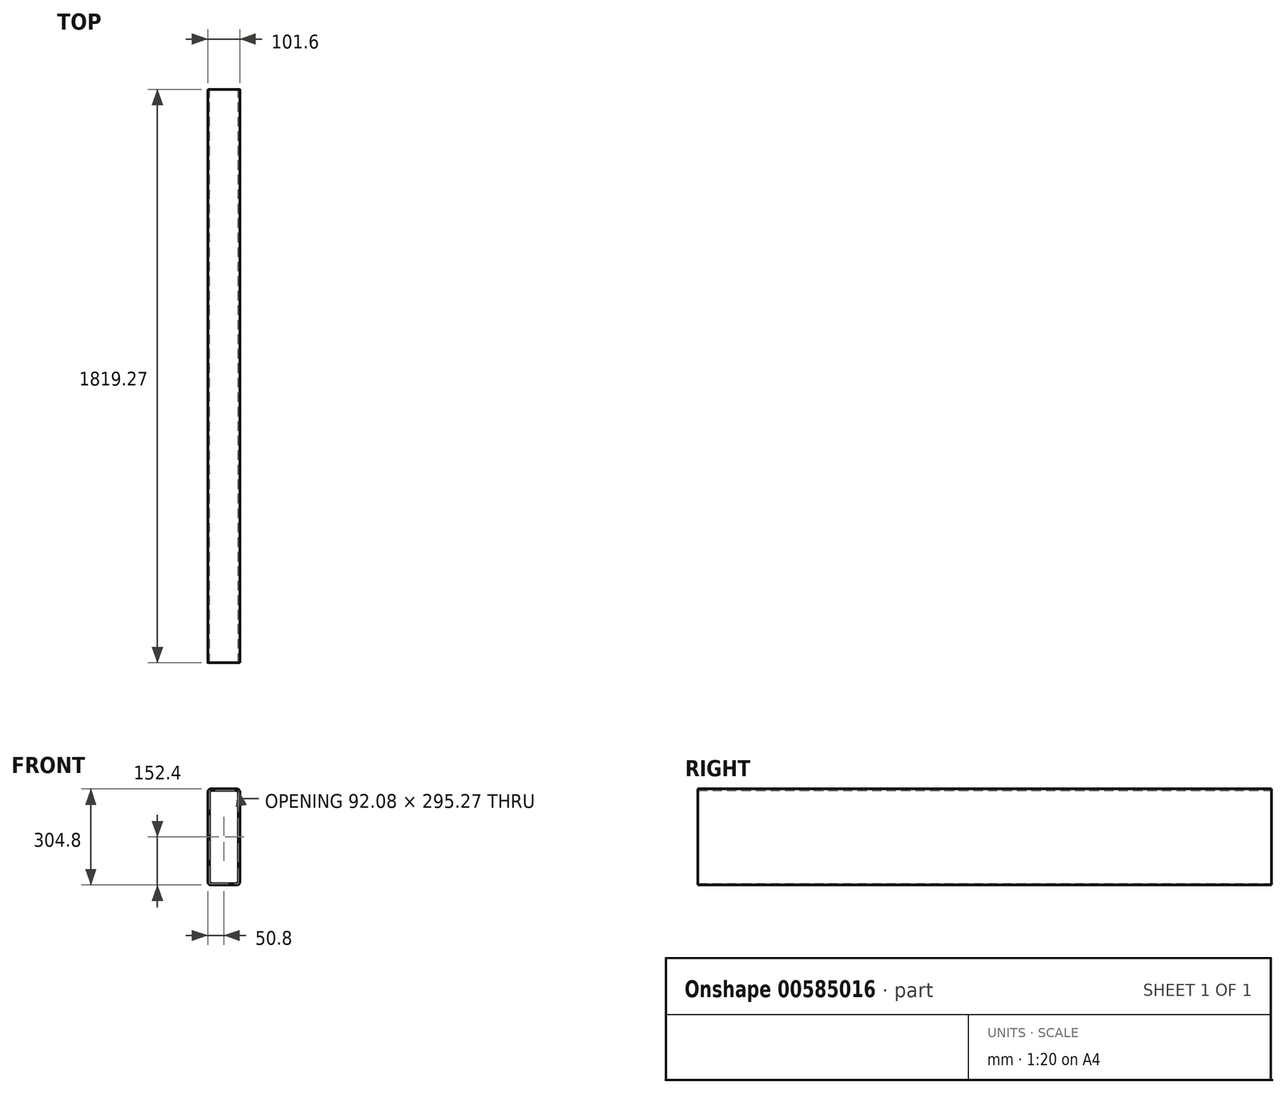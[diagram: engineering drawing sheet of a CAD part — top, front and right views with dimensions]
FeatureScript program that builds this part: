
annotation { "Feature Type Name" : "Feature", "Feature Type Description" : "" }
export const myFeature = defineFeature(function(context is Context, id is Id, definition is map)
    precondition{}
    {
        {
            var Q0;
            Q0=qCreatedBy(makeId("Front.planeOp"),FACE);
            var sketch = newSketch(context, id + "F0", { "sketchPlane" : qUnion([Q0])});
            skLineSegment(sketch, "E0.bottom", {"start": v(50.8, 152.4) * mm, "end": v(-50.8, 152.4) * mm});
            skLineSegment(sketch, "E0.top", {"start": v(50.8, -152.4) * mm, "end": v(-50.8, -152.4) * mm});
            skLineSegment(sketch, "E0.left", {"start": v(50.8, 152.4) * mm, "end": v(50.8, -152.4) * mm});
            skLineSegment(sketch, "E0.right", {"start": v(-50.8, 152.4) * mm, "end": v(-50.8, -152.4) * mm});
            skPoint(sketch, "E0.middle", {"position": v(0, 0) * mm});
            skLineSegment(sketch, "E1.bottom", {"start": v(46.04, 147.64) * mm, "end": v(-46.04, 147.64) * mm});
            skLineSegment(sketch, "E1.top", {"start": v(46.04, -147.64) * mm, "end": v(-46.04, -147.64) * mm});
            skLineSegment(sketch, "E1.left", {"start": v(46.04, 147.64) * mm, "end": v(46.04, -147.64) * mm});
            skLineSegment(sketch, "E1.right", {"start": v(-46.04, 147.64) * mm, "end": v(-46.04, -147.64) * mm});
            skSolve(sketch);
        }
        {
            var Q0;
            Q0 = qSketchRegion(id + "F0", true);
            extrude(context, id + "F1", {"entities" : qUnion([Q0]), "depth" : 1819.27 * mm, "offsetDistance" : 25.4 * mm});
        }
        {
            var Q0;
            Q0=makeQuery(id+"F1.opExtrude","SWEPT_EDGE",EDGE,{"disambiguationData":[OSD([sQuery(id+"F0.wireOp",EDGE,"E0.bottom"),sQuery(id+"F0.wireOp",EDGE,"E0.left")])]});
            var Q1;
            Q1=makeQuery(id+"F1.opExtrude","SWEPT_EDGE",EDGE,{"disambiguationData":[OSD([sQuery(id+"F0.wireOp",EDGE,"E0.bottom"),sQuery(id+"F0.wireOp",EDGE,"E0.right")])]});
            var Q2;
            Q2=makeQuery(id+"F1.opExtrude","SWEPT_EDGE",EDGE,{"disambiguationData":[OSD([sQuery(id+"F0.wireOp",EDGE,"E0.top"),sQuery(id+"F0.wireOp",EDGE,"E0.left")])]});
            var Q3;
            Q3=makeQuery(id+"F1.opExtrude","SWEPT_EDGE",EDGE,{"disambiguationData":[OSD([sQuery(id+"F0.wireOp",EDGE,"E1.top"),sQuery(id+"F0.wireOp",EDGE,"E1.right")])]});
            var Q4;
            Q4=makeQuery(id+"F1.opExtrude","SWEPT_EDGE",EDGE,{"disambiguationData":[OSD([sQuery(id+"F0.wireOp",EDGE,"E0.top"),sQuery(id+"F0.wireOp",EDGE,"E0.right")])]});
            var Q5;
            Q5=makeQuery(id+"F1.opExtrude","SWEPT_EDGE",EDGE,{"disambiguationData":[OSD([sQuery(id+"F0.wireOp",EDGE,"E1.bottom"),sQuery(id+"F0.wireOp",EDGE,"E1.left")])]});
            var Q6;
            Q6=makeQuery(id+"F1.opExtrude","SWEPT_EDGE",EDGE,{"disambiguationData":[OSD([sQuery(id+"F0.wireOp",EDGE,"E1.bottom"),sQuery(id+"F0.wireOp",EDGE,"E1.right")])]});
            var Q7;
            Q7=makeQuery(id+"F1.opExtrude","SWEPT_EDGE",EDGE,{"disambiguationData":[OSD([sQuery(id+"F0.wireOp",EDGE,"E1.top"),sQuery(id+"F0.wireOp",EDGE,"E1.left")])]});
            fillet(context, id + "F2", {"entities" : qUnion([Q0, Q1, Q2, Q3, Q4, Q5, Q6, Q7]), "tangentPropagation" : true, "radius" : 9.52 * mm, "defaultsChanged" : true, "vertexSettings" : [], "allowEdgeOverflow" : false});
        }
    });
